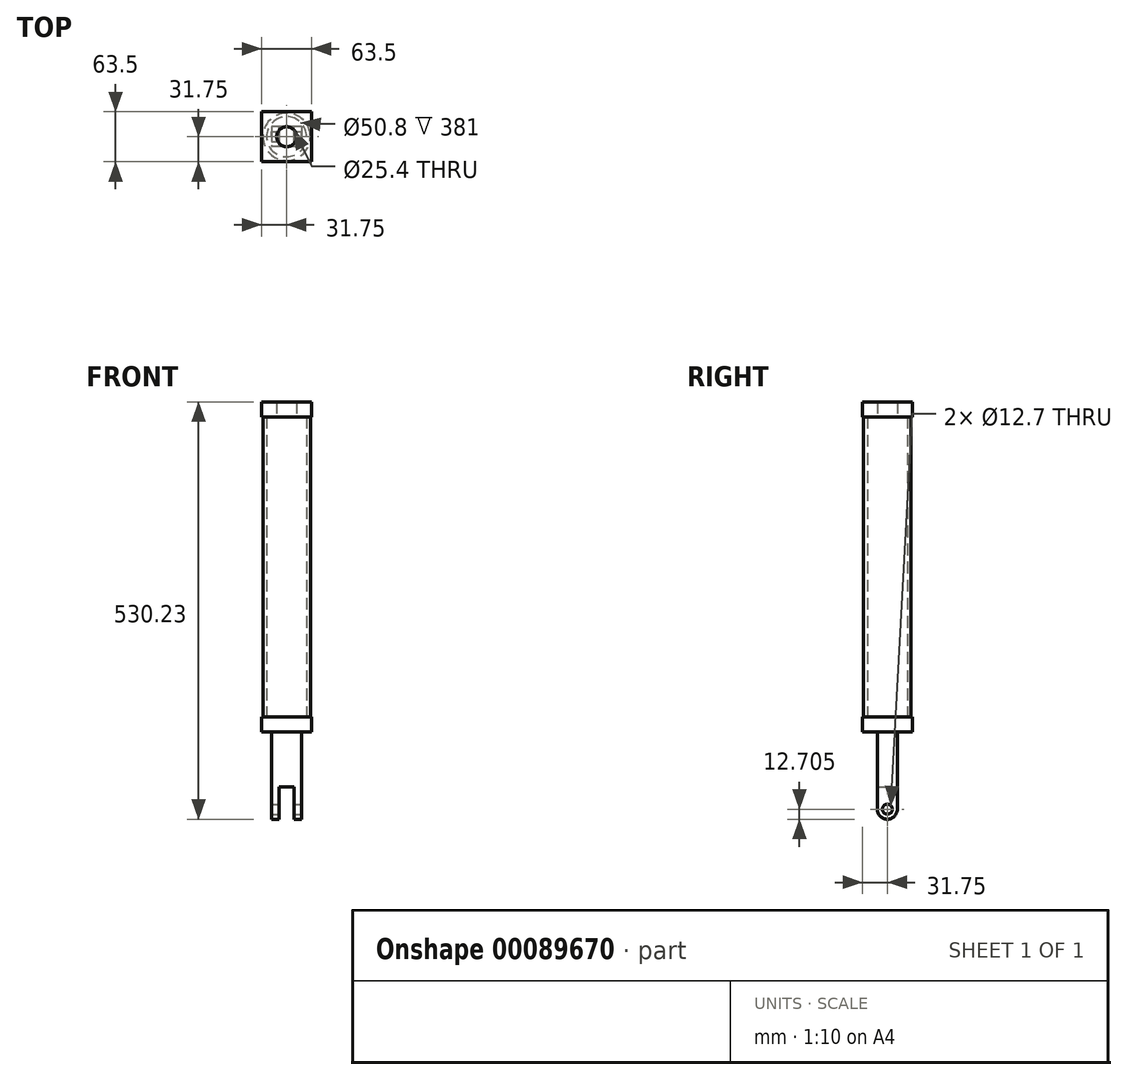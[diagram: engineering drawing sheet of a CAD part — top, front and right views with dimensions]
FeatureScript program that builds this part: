
annotation { "Feature Type Name" : "Feature", "Feature Type Description" : "" }
export const myFeature = defineFeature(function(context is Context, id is Id, definition is map)
    precondition{}
    {
        {
            var Q0;
            Q0=qCreatedBy(makeId("Top.planeOp"),FACE);
            var sketch = newSketch(context, id + "F0", { "sketchPlane" : qUnion([Q0])});
            skCircle(sketch, "E0", {"center": v(0, 0) * mm, "radius": 25.4 * mm});
            skCircle(sketch, "E1", {"center": v(0, 0) * mm, "radius": 30.16 * mm});
            skSolve(sketch);
        }
        {
            var Q0;
            Q0 = qSketchRegion(id + "F0", true);
            extrude(context, id + "F1", {"entities" : qUnion([Q0]), "endBound" : BoundingType.SYMMETRIC, "depth" : 381 * mm});
        }
        {
            var Q0;
            Q0=makeQuery(id+"F1.opExtrude","CAP_FACE",FACE,{"disambiguationData":[OSD([sQuery(id+"F0.wireOp",EDGE,"E0"),sQuery(id+"F0.wireOp",EDGE,"E1")])],"isStart":false});
            cPlane(context, id + "F2", {"entities" : qUnion([Q0]), "cplaneType" : CPlaneType.OFFSET, "offset" : 0 * mm, "width" : 152.4 * mm, "height" : 152.4 * mm});
        }
        {
            var Q0;
            Q0=qCreatedBy(id+"F2.planeOp",FACE);
            var sketch = newSketch(context, id + "F3", { "sketchPlane" : qUnion([Q0])});
            skLineSegment(sketch, "E2.bottom", {"start": v(-31.75, 31.75) * mm, "end": v(31.75, 31.75) * mm});
            skLineSegment(sketch, "E2.top", {"start": v(-31.75, -31.75) * mm, "end": v(31.75, -31.75) * mm});
            skLineSegment(sketch, "E2.left", {"start": v(-31.75, 31.75) * mm, "end": v(-31.75, -31.75) * mm});
            skLineSegment(sketch, "E2.right", {"start": v(31.75, 31.75) * mm, "end": v(31.75, -31.75) * mm});
            skPoint(sketch, "E2.middle", {"position": v(0, 0) * mm});
            skCircle(sketch, "E3", {"center": v(0, 0) * mm, "radius": 12.7 * mm});
            skSolve(sketch);
        }
        {
            var Q0;
            Q0 = qSketchRegion(id + "F3", true);
            extrude(context, id + "F4", {"entities" : qUnion([Q0]), "operationType" : NewBodyOperationType.ADD, "depth" : 19.05 * mm});
        }
        {
            var Q0;
            Q0=makeQuery(id+"F1.opExtrude","CAP_FACE",FACE,{"disambiguationData":[OSD([sQuery(id+"F0.wireOp",EDGE,"E0"),sQuery(id+"F0.wireOp",EDGE,"E1")])],"isStart":true});
            cPlane(context, id + "F5", {"entities" : qUnion([Q0]), "cplaneType" : CPlaneType.OFFSET, "offset" : 0 * mm, "width" : 152.4 * mm, "height" : 152.4 * mm});
        }
        {
            var Q0;
            Q0=qCreatedBy(id+"F5.planeOp",FACE);
            var sketch = newSketch(context, id + "F6", { "sketchPlane" : qUnion([Q0])});
            skLineSegment(sketch, "E4.bottom", {"start": v(-31.75, 31.75) * mm, "end": v(31.75, 31.75) * mm});
            skLineSegment(sketch, "E4.top", {"start": v(-31.75, -31.75) * mm, "end": v(31.75, -31.75) * mm});
            skLineSegment(sketch, "E4.left", {"start": v(-31.75, 31.75) * mm, "end": v(-31.75, -31.75) * mm});
            skLineSegment(sketch, "E4.right", {"start": v(31.75, 31.75) * mm, "end": v(31.75, -31.75) * mm});
            skPoint(sketch, "E4.middle", {"position": v(0, 0) * mm});
            skSolve(sketch);
        }
        {
            var Q0;
            Q0=makeQuery(id+"F6.imprint","IMPRINT",FACE,{"disambiguationData":[TD([[makeQuery(id+"F6.imprint","IMPRINT",EDGE,{"derivedFrom":sQuery(id+"F6.wireOp",EDGE,"E4.bottom")}),-1.0]])]});
            extrude(context, id + "F7", {"entities" : qUnion([Q0]), "operationType" : NewBodyOperationType.ADD, "depth" : 19.05 * mm});
        }
        {
            var Q0;
            Q0=makeQuery(id+"F7.opExtrude","CAP_FACE",FACE,{"disambiguationData":[OSD([sQuery(id+"F6.wireOp",EDGE,"E4.bottom"),sQuery(id+"F6.wireOp",EDGE,"E4.top"),sQuery(id+"F6.wireOp",EDGE,"E4.left"),sQuery(id+"F6.wireOp",EDGE,"E4.right")])],"isStart":false});
            var sketch = newSketch(context, id + "F8", { "sketchPlane" : qUnion([Q0])});
            skLineSegment(sketch, "E5.bottom", {"start": v(19.05, -12.7) * mm, "end": v(-19.05, -12.7) * mm});
            skLineSegment(sketch, "E5.top", {"start": v(19.05, 12.7) * mm, "end": v(-19.05, 12.7) * mm});
            skLineSegment(sketch, "E5.left", {"start": v(19.05, -12.7) * mm, "end": v(19.05, 12.7) * mm});
            skLineSegment(sketch, "E5.right", {"start": v(-19.05, -12.7) * mm, "end": v(-19.05, 12.7) * mm});
            skPoint(sketch, "E5.middle", {"position": v(0, 0) * mm});
            skSolve(sketch);
        }
        {
            var Q0;
            Q0=makeQuery(id+"F8.imprint","IMPRINT",FACE,{"disambiguationData":[TD([[makeQuery(id+"F8.imprint","IMPRINT",EDGE,{"derivedFrom":sQuery(id+"F8.wireOp",EDGE,"E5.bottom")}),-1.0]])]});
            extrude(context, id + "F9", {"entities" : qUnion([Q0]), "operationType" : NewBodyOperationType.ADD, "depth" : 98.42 * mm});
        }
        {
            var Q0;
            Q0=makeQuery(id+"F9.opExtrude","CAP_FACE",FACE,{"disambiguationData":[OSD([sQuery(id+"F8.wireOp",EDGE,"E5.bottom"),sQuery(id+"F8.wireOp",EDGE,"E5.top"),sQuery(id+"F8.wireOp",EDGE,"E5.left"),sQuery(id+"F8.wireOp",EDGE,"E5.right")])],"isStart":false});
            var sketch = newSketch(context, id + "F10", { "sketchPlane" : qUnion([Q0])});
            skLineSegment(sketch, "E6.bottom", {"start": v(-19.05, 12.7) * mm, "end": v(19.05, 12.7) * mm});
            skLineSegment(sketch, "E6.top", {"start": v(-19.05, 0) * mm, "end": v(19.05, 0) * mm});
            skLineSegment(sketch, "E6.left", {"start": v(-19.05, 12.7) * mm, "end": v(-19.05, 0) * mm});
            skLineSegment(sketch, "E6.right", {"start": v(19.05, 12.7) * mm, "end": v(19.05, 0) * mm});
            skSolve(sketch);
        }
        {
            var Q0;
            Q0=makeQuery(id+"F10.imprint","IMPRINT",FACE,{"disambiguationData":[TD([[makeQuery(id+"F10.imprint","IMPRINT",EDGE,{"derivedFrom":sQuery(id+"F10.wireOp",EDGE,"E6.bottom")}),1.0]])]});
            var Q1;
            Q1=sQuery(id+"F10.wireOp",EDGE,"E6.top");
            revolve(context, id + "F11", {"operationType" : NewBodyOperationType.ADD, "entities" : qUnion([Q0]), "axis" : qUnion([Q1]), "revolveType" : RevolveType.FULL});
        }
        {
            var Q0;
            Q0=makeQuery(id+"F11.boolean.opBoolean","MERGE",FACE,{"derivedFrom":[makeQuery(id+"F9.opExtrude","SWEPT_FACE",FACE,{"disambiguationData":[OSD([sQuery(id+"F8.wireOp",EDGE,"E5.left")])]}),makeQuery(id+"F11.opRevolve","SWEPT_FACE",FACE,{"disambiguationData":[OSD([sQuery(id+"F10.wireOp",EDGE,"E6.right")])]})]});
            var sketch = newSketch(context, id + "F12", { "sketchPlane" : qUnion([Q0])});
            skPoint(sketch, "E7", {"position": v(0, -307.98) * mm});
            skSolve(sketch);
        }
        {
            var Q0;
            Q0=sQuery(id+"F12.wireOp",VERTEX,"E7");
            var Q1;
            Q1=makeQuery(id+"F1.opExtrude","SWEPT_BODY",BODY,{"disambiguationData":[OSD([sQuery(id+"F0.wireOp",EDGE,"E0"),sQuery(id+"F0.wireOp",EDGE,"E1")])]});
            hole(context, id + "F13", {"style" : HoleStyle.SIMPLE, "endStyle" : HoleEndStyle.THROUGH, "holeDiameter" : 12.7 * mm, "locations" : qUnion([Q0]), "scope" : qUnion([Q1]), "isTappedThrough" : true});
        }
        {
            var Q0;
            Q0=qCreatedBy(makeId("Right.planeOp"),FACE);
            var sketch = newSketch(context, id + "F14", { "sketchPlane" : qUnion([Q0])});
            skLineSegment(sketch, "E8.bottom", {"start": v(-28.86, -279.4) * mm, "end": v(26.96, -279.4) * mm});
            skLineSegment(sketch, "E8.top", {"start": v(-28.86, -322.08) * mm, "end": v(26.96, -322.08) * mm});
            skLineSegment(sketch, "E8.left", {"start": v(-28.86, -279.4) * mm, "end": v(-28.86, -322.08) * mm});
            skLineSegment(sketch, "E8.right", {"start": v(26.96, -279.4) * mm, "end": v(26.96, -322.08) * mm});
            skSolve(sketch);
        }
        {
            var Q0;
            Q0=makeQuery(id+"F14.imprint","IMPRINT",FACE,{"disambiguationData":[TD([[makeQuery(id+"F14.imprint","IMPRINT",EDGE,{"derivedFrom":sQuery(id+"F14.wireOp",EDGE,"E8.bottom")}),-1.0]])]});
            extrude(context, id + "F15", {"entities" : qUnion([Q0]), "operationType" : NewBodyOperationType.REMOVE, "endBound" : BoundingType.SYMMETRIC, "oppositeDirection" : true, "depth" : 19.05 * mm});
        }
    });
